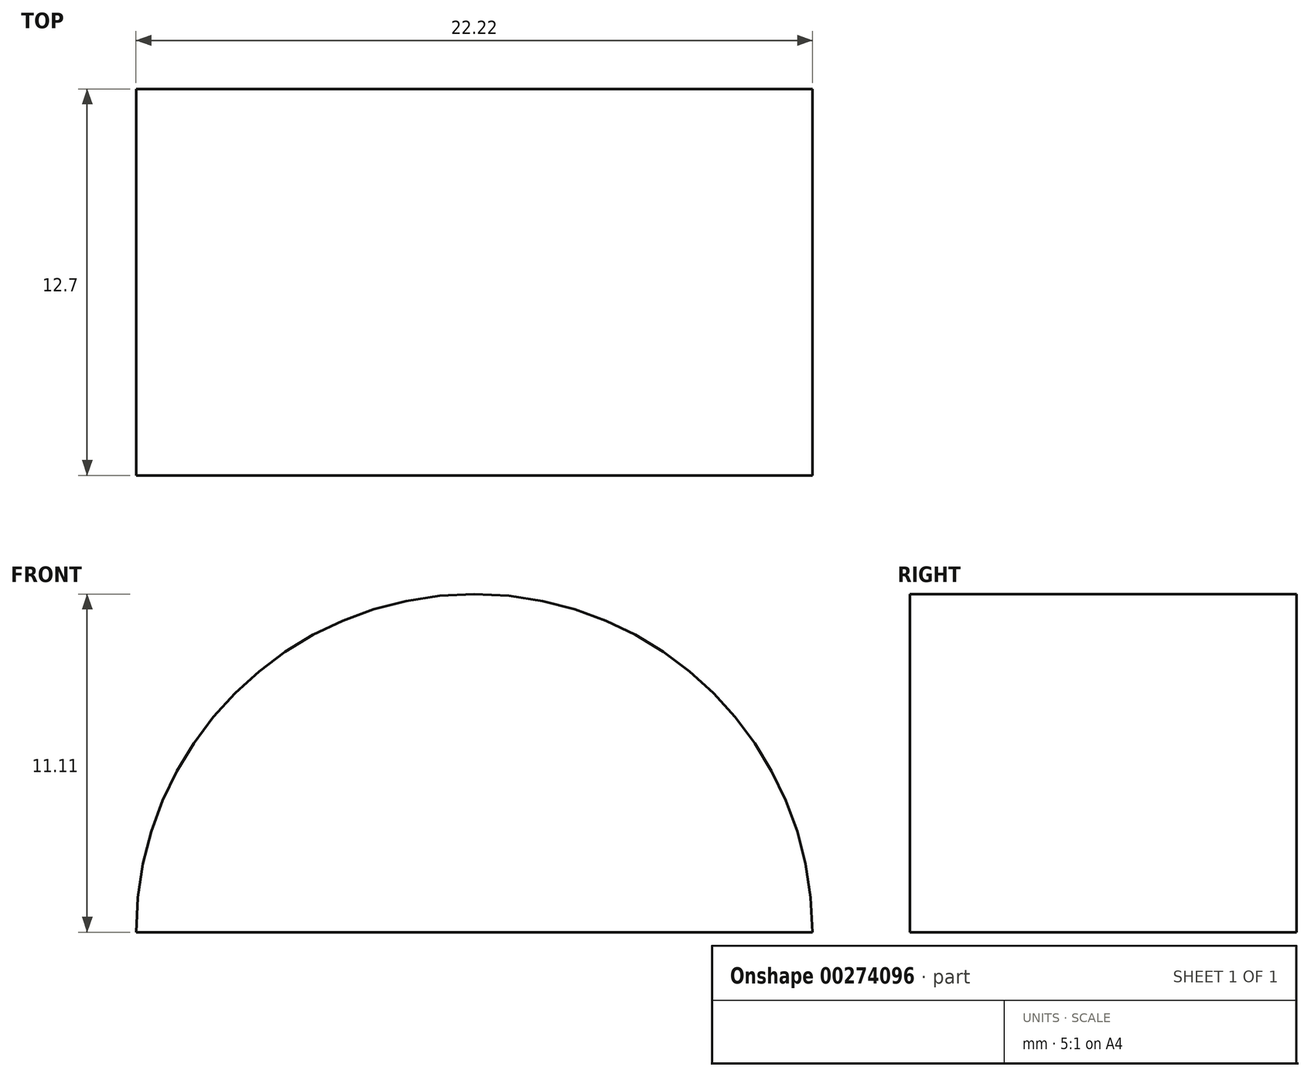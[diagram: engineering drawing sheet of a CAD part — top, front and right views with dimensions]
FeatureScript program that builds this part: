
annotation { "Feature Type Name" : "Feature", "Feature Type Description" : "" }
export const myFeature = defineFeature(function(context is Context, id is Id, definition is map)
    precondition{}
    {
        {
            var Q0;
            Q0=qCreatedBy(makeId("Front.planeOp"),FACE);
            var sketch = newSketch(context, id + "F0", { "sketchPlane" : qUnion([Q0])});
            skLineSegment(sketch, "E0", {"start": v(0, 0) * mm, "end": v(22.86, 0) * mm});
            skArc(sketch, "E1", {"start": v(6.73, 10.07) * mm, "mid": v(17.4, 9.37) * mm, "end": v(22.54, 0) * mm});
            skArc(sketch, "E2", {"start": v(11.43, 11.1) * mm, "mid": v(3.57, 7.86) * mm, "end": v(0.32, 0) * mm});
            skSolve(sketch);
        }
        {
            var Q0;
            Q0 = qSketchRegion(id + "F0", true);
            extrude(context, id + "F1", {"entities" : qUnion([Q0]), "depth" : 12.7 * mm});
        }
    });
